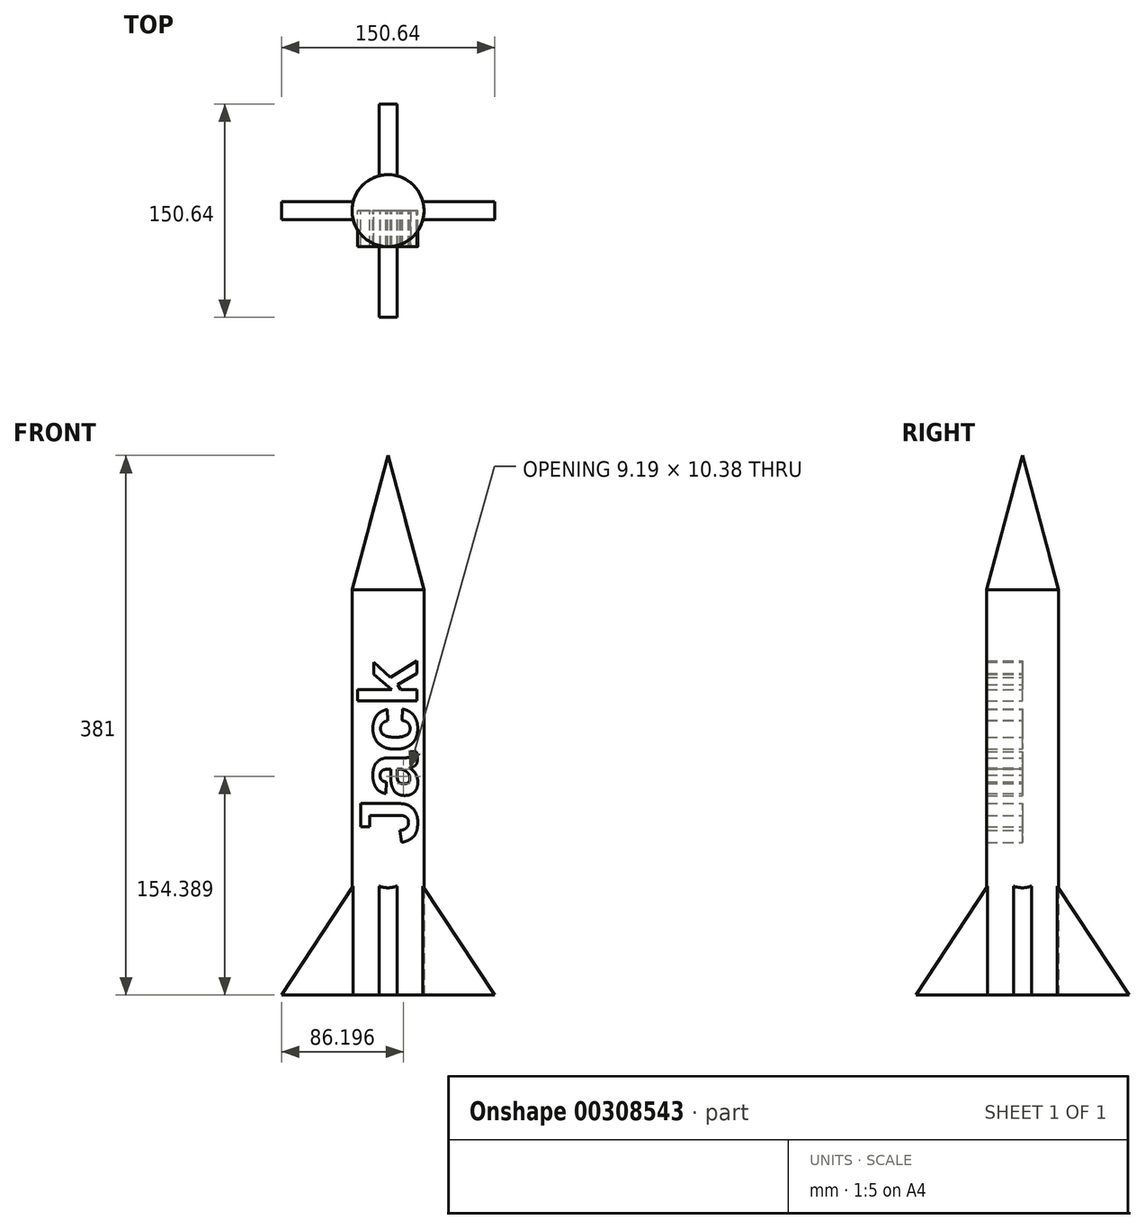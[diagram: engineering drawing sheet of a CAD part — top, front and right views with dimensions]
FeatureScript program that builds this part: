
annotation { "Feature Type Name" : "Feature", "Feature Type Description" : "" }
export const myFeature = defineFeature(function(context is Context, id is Id, definition is map)
    precondition{}
    {
        {
            var Q0;
            Q0=qCreatedBy(makeId("Top.planeOp"),FACE);
            var sketch = newSketch(context, id + "F0", { "sketchPlane" : qUnion([Q0])});
            skCircle(sketch, "E0", {"center": v(0, 0) * mm, "radius": 25.4 * mm});
            skSolve(sketch);
        }
        {
            var Q0;
            Q0=qSketchRegion(id+"F0",true);
            extrude(context, id + "F1", {"entities" : qUnion([Q0]), "depth" : 381 * mm});
        }
        {
            var Q0;
            Q0=makeQuery(id+"F1.opExtrude","CAP_EDGE",EDGE,{"disambiguationData":[OSD([sQuery(id+"F0.wireOp",EDGE,"E0")])],"isStart":false});
            chamfer(context, id + "F2", {"entities" : qUnion([Q0]), "chamferType" : ChamferType.OFFSET_ANGLE, "width" : 25.4 * mm, "oppositeDirection" : false, "angle" : 75 * degree, "tangentPropagation" : true});
        }
        {
            var Q0;
            Q0=qCreatedBy(makeId("Front.planeOp"),FACE);
            var sketch = newSketch(context, id + "F3", { "sketchPlane" : qUnion([Q0])});
            skLineSegment(sketch, "E1", {"start": v(0, 0) * mm, "end": v(0, 114.35) * mm});
            skLineSegment(sketch, "E2", {"start": v(0, 114.35) * mm, "end": v(75.32, 0) * mm});
            skLineSegment(sketch, "E3", {"start": v(0, 0) * mm, "end": v(75.32, 0) * mm});
            skSolve(sketch);
        }
        {
            var Q0;
            Q0=makeQuery(id+"F3.imprint","IMPRINT",FACE,{"disambiguationData":[TD([[makeQuery(id+"F3.imprint","IMPRINT",EDGE,{"derivedFrom":sQuery(id+"F3.wireOp",EDGE,"E1")}),-1.0]])]});
            extrude(context, id + "F4", {"entities" : qUnion([Q0]), "operationType" : NewBodyOperationType.ADD, "endBound" : BoundingType.SYMMETRIC, "depth" : 12.7 * mm});
        }
        {
            var Q0;
            Q0=makeQuery(id+"F1.opExtrude","SWEPT_BODY",BODY,{"disambiguationData":[OSD([sQuery(id+"F0.wireOp",EDGE,"E0")])]});
            var Q1;
            Q1=makeQuery(id+"F1.opExtrude","SWEPT_FACE",FACE,{"disambiguationData":[OSD([sQuery(id+"F0.wireOp",EDGE,"E0")])]});
            circularPattern(context, id + "F5", {"entities" : qUnion([Q0]), "axis" : qUnion([Q1]), "angle" : 360 * degree, "instanceCount" : 4, "equalSpace" : true});
        }
        {
            var Q0;
            Q0=qCreatedBy(makeId("Front.planeOp"),FACE);
            var sketch = newSketch(context, id + "F6", { "sketchPlane" : qUnion([Q0])});
            skText(sketch, "E4", { "text": "Jack", "fontName": "Arimo-Bold.ttf"});
            const initialGuessF6  = {"E4": [0.02045, 0.10701, 0, 1, 0.0417]};
            skSetInitialGuess(sketch, initialGuessF6);
            skSolve(sketch);
        }
        {
            var Q0;
            Q0=qCreatedBy(makeId("Top.planeOp"),FACE);
            var sketch = newSketch(context, id + "F7", { "sketchPlane" : qUnion([Q0])});
            skCircle(sketch, "E5", {"center": v(0, 0) * mm, "radius": 33.36 * mm});
            skSolve(sketch);
        }
        {
            var Q0;
            Q0=sQuery(id+"F7.wireOp",EDGE,"E5");
            extrude(context, id + "F8", {"bodyType" : ToolBodyType.SURFACE, "surfaceEntities" : qUnion([Q0]), "depth" : 25.4 * mm});
        }
        {
            var Q0;
            Q0 = qSketchRegion(id + "F6", true);
            extrude(context, id + "F9", {"entities" : qUnion([Q0]), "depth" : 25.4 * mm});
        }
    });
